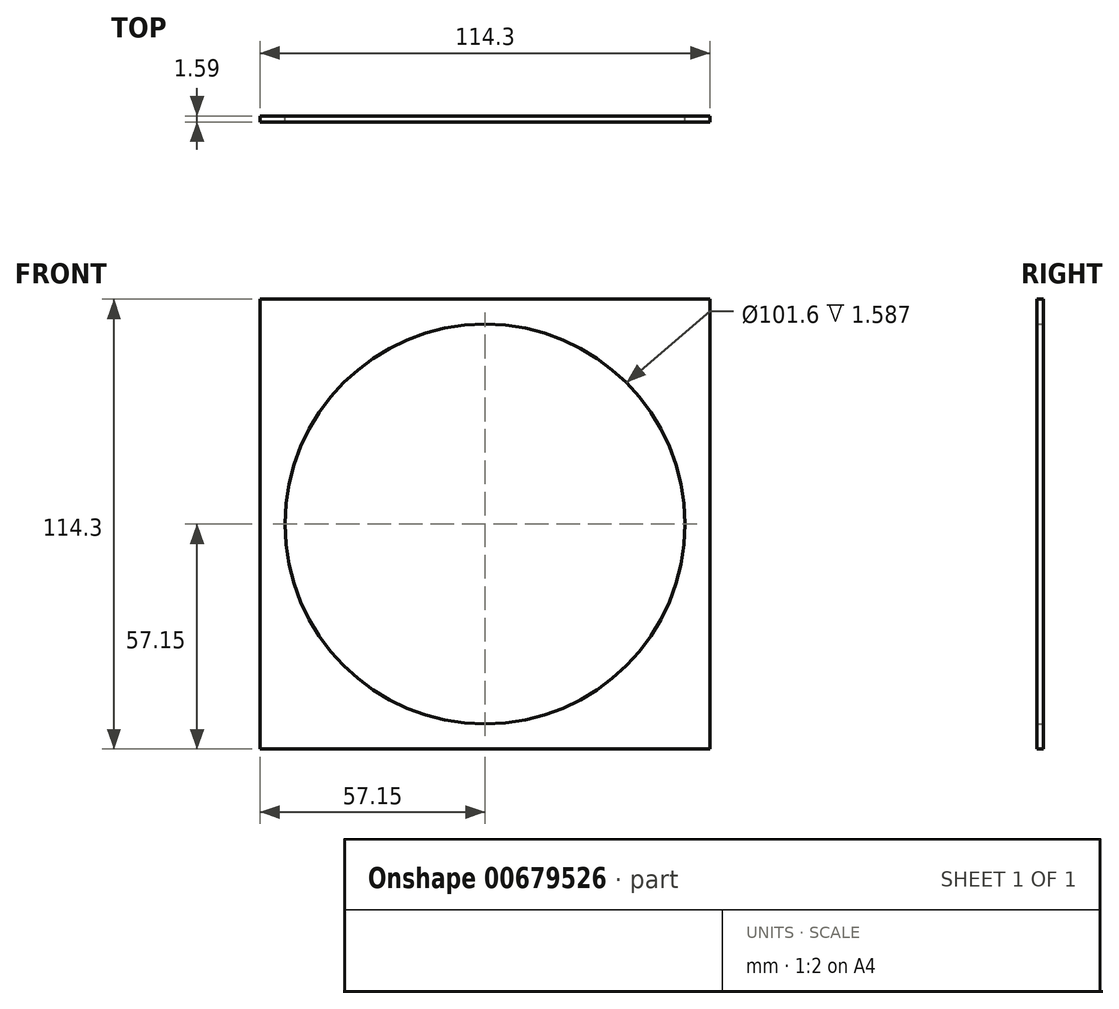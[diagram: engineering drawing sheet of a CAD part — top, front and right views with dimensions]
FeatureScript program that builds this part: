
annotation { "Feature Type Name" : "Feature", "Feature Type Description" : "" }
export const myFeature = defineFeature(function(context is Context, id is Id, definition is map)
    precondition{}
    {
        {
            var Q0;
            Q0=qCreatedBy(makeId("Front.planeOp"),FACE);
            var sketch = newSketch(context, id + "F0", { "sketchPlane" : qUnion([Q0])});
            skLineSegment(sketch, "E0.bottom", {"start": v(-57.15, 57.15) * mm, "end": v(57.15, 57.15) * mm});
            skLineSegment(sketch, "E0.top", {"start": v(-57.15, -57.15) * mm, "end": v(57.15, -57.15) * mm});
            skLineSegment(sketch, "E0.left", {"start": v(-57.15, 57.15) * mm, "end": v(-57.15, -57.15) * mm});
            skLineSegment(sketch, "E0.right", {"start": v(57.15, 57.15) * mm, "end": v(57.15, -57.15) * mm});
            skPoint(sketch, "E0.middle", {"position": v(0, 0) * mm});
            skCircle(sketch, "E1", {"center": v(0, 0) * mm, "radius": 50.8 * mm});
            skSolve(sketch);
        }
        {
            var Q0;
            Q0 = qSketchRegion(id + "F0", true);
            extrude(context, id + "F1", {"entities" : qUnion([Q0]), "depth" : 1.59 * mm, "offsetDistance" : 25.4 * mm});
        }
    });
